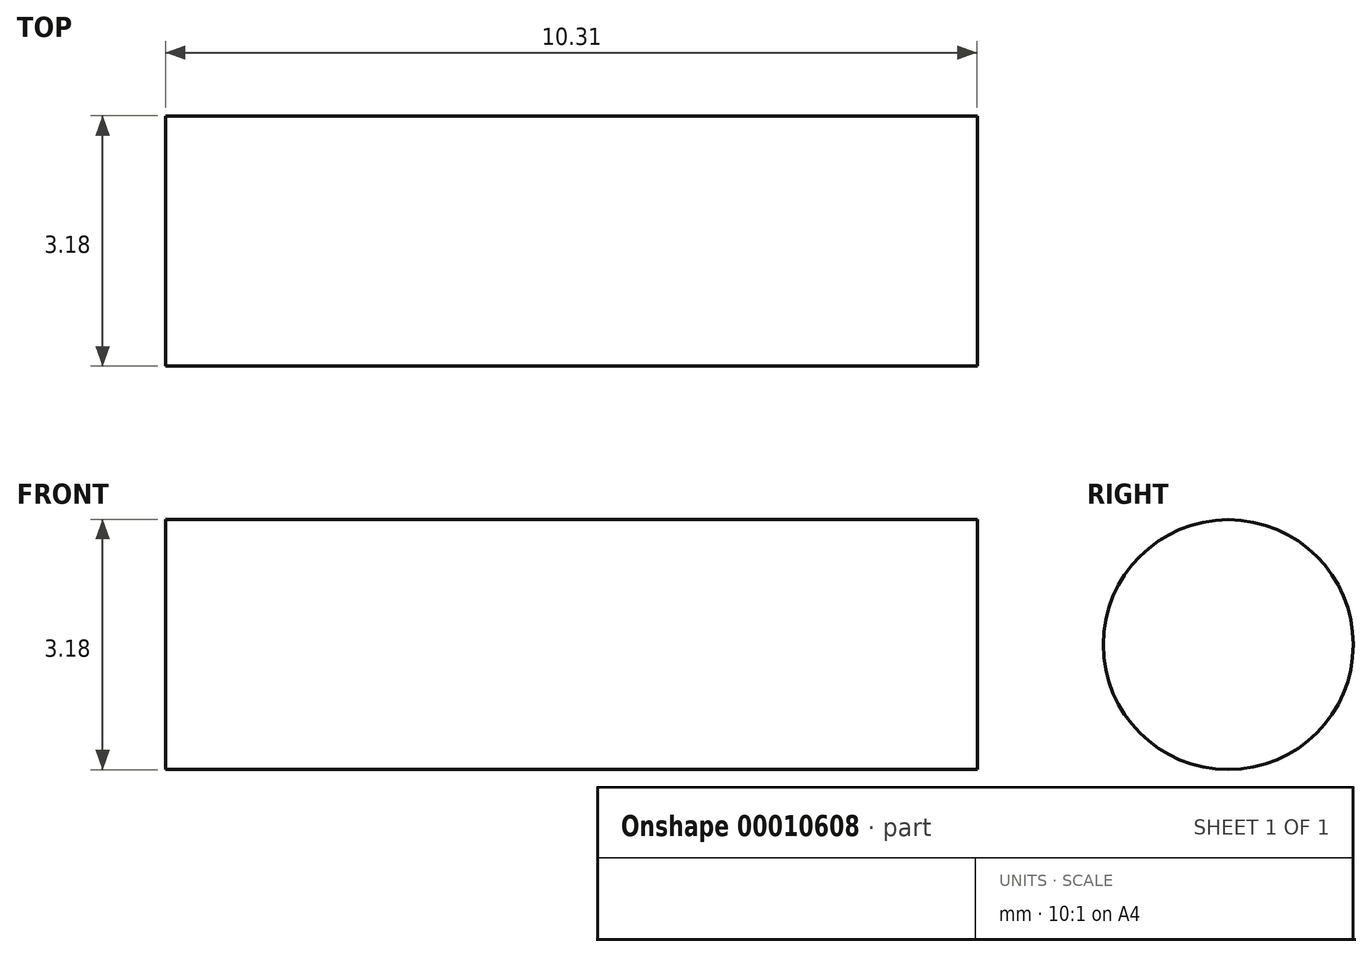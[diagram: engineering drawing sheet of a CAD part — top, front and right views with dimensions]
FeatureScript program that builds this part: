
annotation { "Feature Type Name" : "Feature", "Feature Type Description" : "" }
export const myFeature = defineFeature(function(context is Context, id is Id, definition is map)
    precondition{}
    {
        {
            var Q0;
            Q0=qCreatedBy(makeId("Right.planeOp"),FACE);
            var sketch = newSketch(context, id + "F0", { "sketchPlane" : qUnion([Q0])});
            skCircle(sketch, "E0", {"center": v(0, 0) * mm, "radius": 1.59 * mm});
            skSolve(sketch);
        }
        {
            var Q0;
            Q0=qSketchRegion(id+"F0",true);
            extrude(context, id + "F1", {"entities" : qUnion([Q0]), "depth" : 10.3 * mm});
        }
    });
